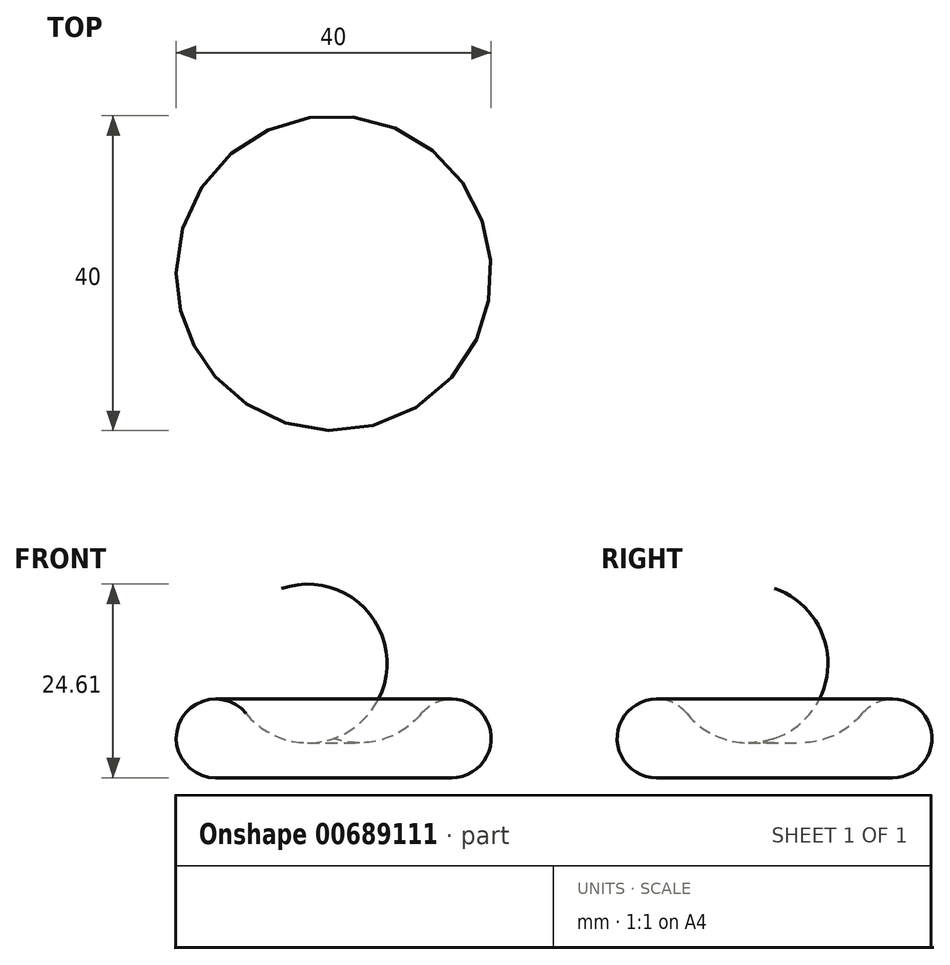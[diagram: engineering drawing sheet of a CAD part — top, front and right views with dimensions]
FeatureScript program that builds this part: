
annotation { "Feature Type Name" : "Feature", "Feature Type Description" : "" }
export const myFeature = defineFeature(function(context is Context, id is Id, definition is map)
    precondition{}
    {
        {
            var Q0;
            Q0=qCreatedBy(makeId("Front.planeOp"),FACE);
            var sketch = newSketch(context, id + "F0", { "sketchPlane" : qUnion([Q0])});
            skArc(sketch, "E0", {"start": v(-11.12, 8.16) * mm, "mid": v(-6.06, 4.83) * mm, "end": v(0, 5) * mm});
            skArc(sketch, "E1", {"start": v(-11.12, 8.16) * mm, "mid": v(-19.52, 7.15) * mm, "end": v(-15, 0) * mm});
            skLineSegment(sketch, "E2", {"start": v(-15, 0) * mm, "end": v(0, 0) * mm});
            skLineSegment(sketch, "E3", {"start": v(0, 0) * mm, "end": v(0, 5) * mm});
            skSolve(sketch);
        }
        {
            var Q0;
            Q0=makeQuery(id+"F0.imprint","IMPRINT",FACE,{"disambiguationData":[TD([[makeQuery(id+"F0.imprint","IMPRINT",EDGE,{"derivedFrom":sQuery(id+"F0.wireOp",EDGE,"E0")}),-1.0]])]});
            var Q1;
            Q1=sQuery(id+"F0.wireOp",EDGE,"E3");
            revolve(context, id + "F1", {"entities" : qUnion([Q0]), "axis" : qUnion([Q1]), "revolveType" : RevolveType.FULL});
        }
        {
            var Q0;
            Q0=qCreatedBy(makeId("Top.planeOp"),FACE);
            cPlane(context, id + "F2", {"entities" : qUnion([Q0]), "cplaneType" : CPlaneType.OFFSET, "offset" : 10 * mm, "width" : 150 * mm, "height" : 150 * mm});
        }
        {
            var Q0;
            Q0=qCreatedBy(makeId("Front.planeOp"),FACE);
            var sketch = newSketch(context, id + "F3", { "sketchPlane" : qUnion([Q0])});
            skCircle(sketch, "E4", {"center": v(-15, 5) * mm, "radius": 4 * mm});
            skSolve(sketch);
        }
        {
            var Q0;
            Q0 = qSketchRegion(id + "F3", true);
            var Q1;
            Q1=sQuery(id+"F0.wireOp",EDGE,"E3");
            revolve(context, id + "F4", {"operationType" : NewBodyOperationType.ADD, "entities" : qUnion([Q0]), "axis" : qUnion([Q1]), "revolveType" : RevolveType.FULL});
        }
    });
